# Revit family: Lighting - Luminii - LineLED - LLHE64 - Array
name_source: partatom
category: Lighting Fixtures
units: mm (PartAtom-declared; Revit-internal decimal feet)

## family parameters
Cut with Voids When Loaded = No
Host = Face
Light Source = No
OmniClass Number = 23.80.70.11.14.21
OmniClass Title = Spots and Tracklight Specialties
Part Type = Normal
Room Calculation Point = No
Round Connector Dimension = Use Diameter
Shared = Yes

## types (2) — shared parameters
Assembly Code = D5020230
C End Caps Width = 3/32"
CCT = 3000K
Current Amps = 50 A
Default Elevation = 0"
Depth = 1/16"
Description = Linear LED strip - 24 VDC
Environment = Indoor
Finish = Metal - Luminii - Silver Anodized Aluminum
Frequency = 60 Hz
Has Battery Backup = No
Has Dimming = Yes
Housing Protection Rating = IP20 Dry/IP66 Wet Series
Initial Color Comments = Perfomance based on 3000K Photometric Web File
Instruction Sheet Link = https://www.luminii.com
Keynote = 26 50 00
Lamp = LED
Lamp Life = 1
Lens Material = Plastic - Luminii - Frosted Lens
Load Classification = Lighting
Manufacturer = Luminii
Mounting Method = Surface Mount
Number of Poles = 1
Operating Temperature = Consult Manufacturer Website for more Information
Phase = 1
Power Factor = 1
Power Source Type = Driver
Product Documentation Link = https://www.luminii.com
Product Name = LineLED HE64
Product Page URL = https://www.luminii.com
URL = https://www.luminii.com
Version = 2020 - v1.0a
Voltage = 24 V
Voltage Comments = 24 VDC
Warranty URL = https://www.luminii.com
Width = 15/32"

## per-type parameters (varying)
| type | Apparent Load | C LED Type | Constraints | Lumen Output | Model | Wattage Comments |
| LineLED HE64 - VHO | 8 VA | Lighting - Luminii - LineLED - LLHE64 - Nested Light Source : LineLED HE64 - VHO | 1 | 986 lm/ft | LLHE64-VHO | 7.5 W/ft |
| LineLED HE64 - XHO | 10 VA | Lighting - Luminii - LineLED - LLHE64 - Nested Light Source : LineLED HE64 - XHO | 2 | 1073 lm/ft | LLHE64-XHO | 9.6 W/ft |

## geometry (parser evidence)
native form markers: Sweep x5
no freeform markers — native parametric forms only
